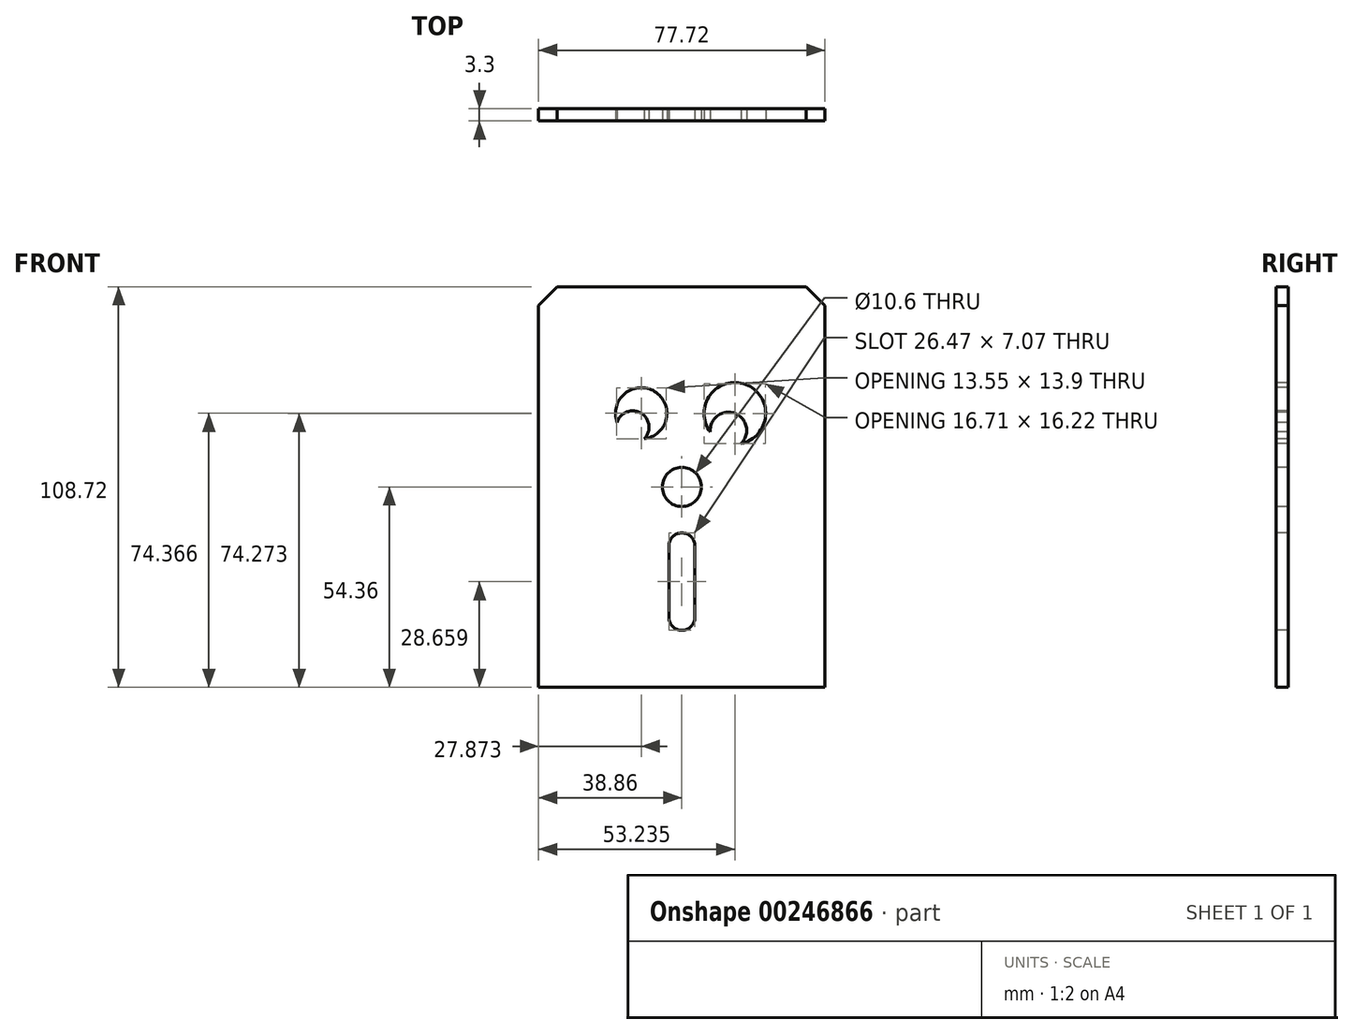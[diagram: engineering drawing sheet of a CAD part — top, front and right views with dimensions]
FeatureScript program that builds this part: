
annotation { "Feature Type Name" : "Feature", "Feature Type Description" : "" }
export const myFeature = defineFeature(function(context is Context, id is Id, definition is map)
    precondition{}
    {
        {
            var Q0;
            Q0=qCreatedBy(makeId("Front.planeOp"),FACE);
            var sketch = newSketch(context, id + "F0", { "sketchPlane" : qUnion([Q0])});
            skLineSegment(sketch, "E0.bottom", {"start": v(38.86, 54.36) * mm, "end": v(-38.86, 54.36) * mm});
            skLineSegment(sketch, "E0.top", {"start": v(38.86, -54.36) * mm, "end": v(-38.86, -54.36) * mm});
            skLineSegment(sketch, "E0.left", {"start": v(38.86, 54.36) * mm, "end": v(38.86, -54.36) * mm});
            skLineSegment(sketch, "E0.right", {"start": v(-38.86, 54.36) * mm, "end": v(-38.86, -54.36) * mm});
            skPoint(sketch, "E0.middle", {"position": v(0, 0) * mm});
            skSolve(sketch);
        }
        {
            var Q0;
            Q0=qSketchRegion(id+"F0",true);
            extrude(context, id + "F1", {"entities" : qUnion([Q0]), "depth" : 3.3 * mm});
        }
        {
            var Q0;
            Q0=makeQuery(id+"F1.opExtrude","CAP_FACE",FACE,{"disambiguationData":[OSD([sQuery(id+"F0.wireOp",EDGE,"E0.bottom"),sQuery(id+"F0.wireOp",EDGE,"E0.top"),sQuery(id+"F0.wireOp",EDGE,"E0.left"),sQuery(id+"F0.wireOp",EDGE,"E0.right")])],"isStart":false});
            var sketch = newSketch(context, id + "F2", { "sketchPlane" : qUnion([Q0])});
            skLineSegment(sketch, "E1", {"start": v(0, 57.24) * mm, "end": v(0, -57.24) * mm, "construction": true});
            skLineSegment(sketch, "E2", {"start": v(-50.8, 0) * mm, "end": v(50.8, 0) * mm, "construction": true});
            skArc(sketch, "E3", {"start": v(35.44, -3.57) * mm, "mid": v(31.46, -11.87) * mm, "end": v(32.26, -21.03) * mm});
            skLineSegment(sketch, "E4", {"start": v(15.88, -44.54) * mm, "end": v(0, -44.54) * mm, "construction": true});
            skArc(sketch, "E5", {"start": v(15.88, -44.54) * mm, "mid": v(30.2, -37.06) * mm, "end": v(32.26, -21.03) * mm});
            skArc(sketch, "E6", {"start": v(15.88, -44.54) * mm, "mid": v(7.78, -45.34) * mm, "end": v(0, -47.71) * mm});
            skArc(sketch, "E7.MirrorCS", {"start": v(-15.87, -44.54) * mm, "mid": v(-7.78, -45.34) * mm, "end": v(0, -47.71) * mm});
            skArc(sketch, "E8.MirrorCS", {"start": v(-15.87, -44.54) * mm, "mid": v(-30.2, -37.06) * mm, "end": v(-32.26, -21.03) * mm});
            skArc(sketch, "E9.MirrorCS", {"start": v(-35.44, -3.57) * mm, "mid": v(-31.46, -11.87) * mm, "end": v(-32.26, -21.03) * mm});
            skArc(sketch, "E10.MirrorCS", {"start": v(-35.44, 3.57) * mm, "mid": v(-31.46, 11.87) * mm, "end": v(-32.26, 21.03) * mm});
            skArc(sketch, "E11.MirrorCS", {"start": v(-15.88, 44.54) * mm, "mid": v(-30.2, 37.06) * mm, "end": v(-32.26, 21.03) * mm});
            skArc(sketch, "E12.MirrorCS", {"start": v(-15.88, 44.54) * mm, "mid": v(-7.78, 45.34) * mm, "end": v(0, 47.71) * mm});
            skArc(sketch, "E13.MirrorCS", {"start": v(15.87, 44.54) * mm, "mid": v(7.78, 45.34) * mm, "end": v(0, 47.71) * mm});
            skArc(sketch, "E14.MirrorCS", {"start": v(15.87, 44.54) * mm, "mid": v(30.2, 37.06) * mm, "end": v(32.26, 21.03) * mm});
            skArc(sketch, "E15.MirrorCS", {"start": v(35.44, 3.57) * mm, "mid": v(31.46, 11.87) * mm, "end": v(32.26, 21.03) * mm});
            skArc(sketch, "E16", {"start": v(35.44, 3.57) * mm, "mid": v(34.41, 0) * mm, "end": v(35.44, -3.57) * mm});
            skPoint(sketch, "E17.orphan", {"position": v(39.69, 0) * mm});
            skArc(sketch, "E18.MirrorCS", {"start": v(-35.44, 3.57) * mm, "mid": v(-34.41, 0) * mm, "end": v(-35.44, -3.57) * mm});
            skPoint(sketch, "E19.orphan", {"position": v(-39.69, 0) * mm});
            skSolve(sketch);
        }
        {
            var Q0;
            Q0=makeQuery(id+"F2.imprint","IMPRINT",FACE,{"disambiguationData":[TD([[makeQuery(id+"F2.imprint","IMPRINT",EDGE,{"derivedFrom":sQuery(id+"F2.wireOp",EDGE,"E3")}),1.0]])]});
            var sketch = newSketch(context, id + "F3", { "sketchPlane" : qUnion([Q0])});
            skFitSpline(sketch, "E20", {"points": [v(-34.74, -25) * mm, v(-17.68, -23.14) * mm, v(0, -25.84) * mm, v(18.3, -28) * mm, v(33.6, -24.4) * mm], "startDerivative": vector(68.08, 28.42) * mm, "endDerivative": vector(41.75, 55.86) * mm});
            skArc(sketch, "E21.0", {"start": v(15.88, -44.54) * mm, "mid": v(28.97, -38.63) * mm, "end": v(33.2, -24.9) * mm});
            skArc(sketch, "E22.0", {"start": v(-15.87, -44.54) * mm, "mid": v(-29.14, -38.43) * mm, "end": v(-33.13, -24.38) * mm});
            skArc(sketch, "E23.0", {"start": v(15.88, -44.54) * mm, "mid": v(7.78, -45.34) * mm, "end": v(0, -47.71) * mm});
            skArc(sketch, "E23.1", {"start": v(-15.87, -44.54) * mm, "mid": v(-7.78, -45.34) * mm, "end": v(0, -47.71) * mm});
            skPoint(sketch, "E24.orphan", {"position": v(-32.26, -21.03) * mm});
            skLineSegment(sketch, "E25.bottom", {"start": v(23.58, -32.65) * mm, "end": v(5.44, -32.65) * mm, "construction": true});
            skLineSegment(sketch, "E25.top", {"start": v(23.58, -12.55) * mm, "end": v(5.44, -12.55) * mm, "construction": true});
            skLineSegment(sketch, "E25.left", {"start": v(23.58, -32.65) * mm, "end": v(23.58, -12.55) * mm, "construction": true});
            skLineSegment(sketch, "E25.right", {"start": v(5.44, -32.65) * mm, "end": v(5.44, -12.55) * mm, "construction": true});
            skArc(sketch, "E26", {"start": v(6.5, -26.77) * mm, "mid": v(6.6, -19.6) * mm, "end": v(5.44, -12.55) * mm});
            skArc(sketch, "E27", {"start": v(23.58, -12.55) * mm, "mid": v(22.47, -20.37) * mm, "end": v(22.78, -28.26) * mm});
            skLineSegment(sketch, "E28", {"start": v(0.57, -13.45) * mm, "end": v(5.44, -12.55) * mm});
            skLineSegment(sketch, "E29", {"start": v(28.46, 0) * mm, "end": v(0.57, 0) * mm, "construction": true});
            skArc(sketch, "E30", {"start": v(-2.4, -8.48) * mm, "mid": v(-2.65, -12) * mm, "end": v(0.57, -13.45) * mm});
            skArc(sketch, "E31", {"start": v(0, -10.42) * mm, "mid": v(-0.23, -8.24) * mm, "end": v(-2.4, -8.48) * mm});
            skArc(sketch, "E32", {"start": v(0, -10.42) * mm, "mid": v(-0.04, -11.92) * mm, "end": v(1.4, -12.35) * mm});
            skArc(sketch, "E33", {"start": v(1.4, -12.35) * mm, "mid": v(5.55, -5.86) * mm, "end": v(0.57, 0) * mm});
            skLineSegment(sketch, "E34", {"start": v(14.51, 0) * mm, "end": v(14.51, -12.55) * mm, "construction": true});
            skArc(sketch, "E35.MirrorCS", {"start": v(27.61, -12.35) * mm, "mid": v(23.47, -5.86) * mm, "end": v(28.46, 0) * mm});
            skLineSegment(sketch, "E36.MirrorCS", {"start": v(28.46, -13.45) * mm, "end": v(23.58, -12.55) * mm});
            skArc(sketch, "E37.MirrorCS", {"start": v(31.42, -8.48) * mm, "mid": v(31.67, -12) * mm, "end": v(28.46, -13.45) * mm});
            skArc(sketch, "E38.MirrorCS", {"start": v(29.02, -10.42) * mm, "mid": v(29.25, -8.24) * mm, "end": v(31.42, -8.48) * mm});
            skArc(sketch, "E39.MirrorCS", {"start": v(29.02, -10.42) * mm, "mid": v(29.06, -11.92) * mm, "end": v(27.61, -12.35) * mm});
            skArc(sketch, "E40", {"start": v(0.57, 0) * mm, "mid": v(5.65, -0.6) * mm, "end": v(10.76, -0.93) * mm});
            skLineSegment(sketch, "E41", {"start": v(10.76, -0.93) * mm, "end": v(8.47, 9.06) * mm});
            skLineSegment(sketch, "E42", {"start": v(8.47, 9.06) * mm, "end": v(6.8, 8.68) * mm});
            skArc(sketch, "E43", {"start": v(7.7, 9.94) * mm, "mid": v(5.6, 10.49) * mm, "end": v(6.8, 8.68) * mm});
            skLineSegment(sketch, "E44", {"start": v(14.51, 0) * mm, "end": v(14.77, 8.31) * mm, "construction": true});
            skLineSegment(sketch, "E45.MirrorCS", {"start": v(18.26, -0.93) * mm, "end": v(21.1, 8.66) * mm});
            skLineSegment(sketch, "E46.MirrorCS", {"start": v(21.1, 8.66) * mm, "end": v(22.75, 8.18) * mm});
            skArc(sketch, "E47.MirrorCS", {"start": v(21.93, 9.5) * mm, "mid": v(24.07, 9.9) * mm, "end": v(22.75, 8.18) * mm});
            skArc(sketch, "E48", {"start": v(7.7, 9.94) * mm, "mid": v(12.62, 15.22) * mm, "end": v(14.1, 22.28) * mm});
            skArc(sketch, "E49", {"start": v(15.59, 22.28) * mm, "mid": v(17.1, 15.06) * mm, "end": v(21.93, 9.5) * mm});
            skLineSegment(sketch, "E50", {"start": v(14.1, 22.28) * mm, "end": v(12.75, 29.94) * mm});
            skLineSegment(sketch, "E51", {"start": v(12.75, 29.94) * mm, "end": v(10.25, 29.5) * mm});
            skLineSegment(sketch, "E52", {"start": v(10.25, 29.5) * mm, "end": v(10.04, 30.72) * mm});
            skLineSegment(sketch, "E53", {"start": v(10.04, 30.72) * mm, "end": v(12.66, 31.3) * mm});
            skLineSegment(sketch, "E54", {"start": v(12.66, 31.3) * mm, "end": v(12.12, 34.79) * mm});
            skLineSegment(sketch, "E55", {"start": v(12.12, 34.79) * mm, "end": v(14.24, 35.11) * mm});
            skLineSegment(sketch, "E56", {"start": v(14.24, 35.11) * mm, "end": v(14.8, 31.45) * mm});
            skLineSegment(sketch, "E57", {"start": v(14.8, 31.45) * mm, "end": v(17.72, 31.9) * mm});
            skLineSegment(sketch, "E58", {"start": v(17.72, 31.9) * mm, "end": v(17.99, 30.17) * mm});
            skLineSegment(sketch, "E59", {"start": v(17.99, 30.17) * mm, "end": v(14.89, 29.68) * mm});
            skLineSegment(sketch, "E60", {"start": v(14.89, 29.68) * mm, "end": v(15.59, 22.28) * mm});
            skArc(sketch, "E61.trimOffspring", {"start": v(18.26, -0.93) * mm, "mid": v(23.37, -0.6) * mm, "end": v(28.46, 0) * mm});
            skPoint(sketch, "E62.orphan", {"position": v(18.2, -1.17) * mm});
            skLineSegment(sketch, "E63", {"start": v(8.48, -4.98) * mm, "end": v(9.12, -7.41) * mm});
            skLineSegment(sketch, "E64", {"start": v(9.77, -9.85) * mm, "end": v(10.94, -9.54) * mm});
            skLineSegment(sketch, "E65", {"start": v(12.72, -9.06) * mm, "end": v(12.26, -7.34) * mm});
            skLineSegment(sketch, "E66", {"start": v(11.56, -4.7) * mm, "end": v(10.33, -4.82) * mm});
            skLineSegment(sketch, "E67", {"start": v(9.75, -4.87) * mm, "end": v(10.34, -7.13) * mm});
            skLineSegment(sketch, "E68", {"start": v(10.34, -7.13) * mm, "end": v(9.12, -7.41) * mm});
            skLineSegment(sketch, "E69", {"start": v(10.33, -4.82) * mm, "end": v(10.9, -7.06) * mm});
            skLineSegment(sketch, "E70", {"start": v(10.9, -7.06) * mm, "end": v(12.14, -6.89) * mm});
            skLineSegment(sketch, "E71", {"start": v(9.29, -8.05) * mm, "end": v(10.46, -7.73) * mm});
            skLineSegment(sketch, "E72", {"start": v(10.46, -7.73) * mm, "end": v(10.94, -9.54) * mm});
            skLineSegment(sketch, "E73", {"start": v(11.57, -9.37) * mm, "end": v(11.12, -7.64) * mm});
            skLineSegment(sketch, "E74", {"start": v(11.12, -7.64) * mm, "end": v(12.26, -7.34) * mm});
            skLineSegment(sketch, "E75.trimOffspring", {"start": v(12.14, -6.89) * mm, "end": v(11.56, -4.7) * mm});
            skLineSegment(sketch, "E76.trimOffspring", {"start": v(9.75, -4.87) * mm, "end": v(8.48, -4.98) * mm});
            skLineSegment(sketch, "E77.trimOffspring", {"start": v(9.29, -8.05) * mm, "end": v(9.77, -9.85) * mm});
            skLineSegment(sketch, "E78.trimOffspring", {"start": v(11.57, -9.37) * mm, "end": v(12.72, -9.06) * mm});
            skLineSegment(sketch, "E79.MirrorCS", {"start": v(17.46, -4.7) * mm, "end": v(18.69, -4.82) * mm});
            skLineSegment(sketch, "E80.MirrorCS", {"start": v(19.27, -4.87) * mm, "end": v(18.68, -7.13) * mm});
            skLineSegment(sketch, "E81.MirrorCS", {"start": v(17.45, -9.37) * mm, "end": v(17.9, -7.64) * mm});
            skLineSegment(sketch, "E82.MirrorCS", {"start": v(18.68, -7.13) * mm, "end": v(19.9, -7.41) * mm});
            skLineSegment(sketch, "E83.MirrorCS", {"start": v(17.9, -7.64) * mm, "end": v(16.76, -7.34) * mm});
            skLineSegment(sketch, "E84.MirrorCS", {"start": v(18.69, -4.82) * mm, "end": v(18.12, -7.06) * mm});
            skLineSegment(sketch, "E85.MirrorCS", {"start": v(16.88, -6.89) * mm, "end": v(17.46, -4.7) * mm});
            skLineSegment(sketch, "E86.MirrorCS", {"start": v(18.12, -7.06) * mm, "end": v(16.88, -6.89) * mm});
            skLineSegment(sketch, "E87.MirrorCS", {"start": v(19.27, -4.87) * mm, "end": v(20.54, -4.98) * mm});
            skLineSegment(sketch, "E88.MirrorCS", {"start": v(20.54, -4.98) * mm, "end": v(19.9, -7.41) * mm});
            skLineSegment(sketch, "E89.MirrorCS", {"start": v(19.73, -8.05) * mm, "end": v(18.56, -7.73) * mm});
            skLineSegment(sketch, "E90.MirrorCS", {"start": v(19.73, -8.05) * mm, "end": v(19.25, -9.85) * mm});
            skLineSegment(sketch, "E91.MirrorCS", {"start": v(19.25, -9.85) * mm, "end": v(18.08, -9.54) * mm});
            skLineSegment(sketch, "E92.MirrorCS", {"start": v(18.56, -7.73) * mm, "end": v(18.08, -9.54) * mm});
            skLineSegment(sketch, "E93.MirrorCS", {"start": v(17.45, -9.37) * mm, "end": v(16.3, -9.06) * mm});
            skLineSegment(sketch, "E94.MirrorCS", {"start": v(16.3, -9.06) * mm, "end": v(16.76, -7.34) * mm});
            skArc(sketch, "E95", {"start": v(14.28, 11.97) * mm, "mid": v(12.23, 10.98) * mm, "end": v(11.15, 8.98) * mm});
            skLineSegment(sketch, "E96", {"start": v(14.28, 11.97) * mm, "end": v(14.28, 8.98) * mm});
            skLineSegment(sketch, "E97", {"start": v(15.17, 4.65) * mm, "end": v(15.17, 7.88) * mm});
            skLineSegment(sketch, "E98", {"start": v(18.4, 8.98) * mm, "end": v(15.17, 8.98) * mm});
            skLineSegment(sketch, "E99", {"start": v(11.1, 7.88) * mm, "end": v(14.28, 7.88) * mm});
            skLineSegment(sketch, "E100.trimOffspring", {"start": v(15.17, 8.98) * mm, "end": v(15.17, 11.98) * mm});
            skLineSegment(sketch, "E101.trimOffspring", {"start": v(15.17, 7.88) * mm, "end": v(18.43, 7.88) * mm});
            skLineSegment(sketch, "E102.trimOffspring", {"start": v(14.28, 7.88) * mm, "end": v(14.28, 4.66) * mm});
            skLineSegment(sketch, "E103.trimOffspring", {"start": v(14.28, 8.98) * mm, "end": v(11.15, 8.98) * mm});
            skArc(sketch, "E104.trimOffspring", {"start": v(11.1, 7.88) * mm, "mid": v(12.14, 5.73) * mm, "end": v(14.28, 4.66) * mm});
            skArc(sketch, "E105.trimOffspring", {"start": v(18.4, 8.98) * mm, "mid": v(17.28, 11.01) * mm, "end": v(15.17, 11.98) * mm});
            skArc(sketch, "E106.trimOffspring", {"start": v(15.17, 4.65) * mm, "mid": v(17.37, 5.7) * mm, "end": v(18.43, 7.88) * mm});
            skLineSegment(sketch, "E107.left", {"start": v(12.04, -27.4) * mm, "end": v(12.04, -21.48) * mm});
            skLineSegment(sketch, "E107.right", {"start": v(16, -27.8) * mm, "end": v(16, -21.48) * mm});
            skArc(sketch, "E108", {"start": v(16, -21.48) * mm, "mid": v(14.02, -19.5) * mm, "end": v(12.04, -21.48) * mm});
            skLineSegment(sketch, "E109", {"start": v(12.04, -27.4) * mm, "end": v(16, -27.8) * mm});
            skArc(sketch, "E110.0", {"start": v(-35.44, -3.57) * mm, "mid": v(-31.46, -11.87) * mm, "end": v(-32.26, -21.03) * mm, "construction": true});
            skArc(sketch, "E110.1", {"start": v(15.87, 44.54) * mm, "mid": v(7.78, 45.34) * mm, "end": v(0, 47.71) * mm});
            skArc(sketch, "E110.2", {"start": v(-15.88, 44.54) * mm, "mid": v(-30.2, 37.06) * mm, "end": v(-32.26, 21.03) * mm, "construction": true});
            skArc(sketch, "E110.3", {"start": v(-35.44, 3.57) * mm, "mid": v(-34.41, 0) * mm, "end": v(-35.44, -3.57) * mm, "construction": true});
            skArc(sketch, "E110.4", {"start": v(-35.44, 3.57) * mm, "mid": v(-31.46, 11.87) * mm, "end": v(-32.26, 21.03) * mm});
            skArc(sketch, "E110.5", {"start": v(-15.88, 44.54) * mm, "mid": v(-7.78, 45.34) * mm, "end": v(0, 47.71) * mm});
            skArc(sketch, "E111", {"start": v(-17.1, 9.66) * mm, "mid": v(-3.37, 14.89) * mm, "end": v(1.5, 28.74) * mm});
            skArc(sketch, "E112", {"start": v(-17.1, 9.66) * mm, "mid": v(-26.87, 8.42) * mm, "end": v(-35.44, 3.57) * mm});
            skArc(sketch, "E113", {"start": v(15.87, 44.54) * mm, "mid": v(5.2, 39.82) * mm, "end": v(1.5, 28.74) * mm});
            skArc(sketch, "E114.trimOffspring", {"start": v(-15.88, 44.54) * mm, "mid": v(-30.2, 37.06) * mm, "end": v(-32.26, 21.03) * mm});
            skArc(sketch, "E115", {"start": v(-24.92, -22.89) * mm, "mid": v(-23.55, -16.2) * mm, "end": v(-24.4, -9.44) * mm});
            skFitSpline(sketch, "E116", {"points": [v(-24.4, -9.44) * mm, v(-26.98, -10.38) * mm, v(-27.97, -8.39) * mm, v(-29.93, -8.52) * mm, v(-30.92, -6) * mm, v(-32.1, -5.52) * mm, v(-32.53, -4.18) * mm, v(-32.18, -3.27) * mm, v(-31.84, -4.44) * mm, v(-31.05, -4.83) * mm, v(-31.49, -2) * mm, v(-30.88, -2.14) * mm, v(-30.1, -5.05) * mm, v(-29.45, -3.57) * mm, v(-28.71, -3.66) * mm, v(-29.54, -5.78) * mm, v(-29.23, -7.17) * mm, v(-27.54, -7.04) * mm, v(-26.28, -8.52) * mm, v(-24.4, -7.6) * mm], "startDerivative": vector(-46.53, -30.94) * mm, "endDerivative": vector(36.03, 29.74) * mm});
            skArc(sketch, "E117", {"start": v(-24.4, -7.6) * mm, "mid": v(-24.93, -4.98) * mm, "end": v(-25.9, -2.49) * mm});
            skFitSpline(sketch, "E118", {"points": [v(-25.9, -2.49) * mm, v(-27.5, -1.49) * mm, v(-28.76, -1.49) * mm, v(-29.23, 0) * mm, v(-31.14, 0) * mm, v(-30.8, 3.42) * mm, v(-29.97, 3.55) * mm, v(-30.27, 1.77) * mm, v(-29.54, 1.72) * mm, v(-28.8, 4.59) * mm, v(-27.67, 4.37) * mm, v(-28.28, 1.98) * mm, v(-27.84, 0) * mm, v(-27.2, 2.46) * mm, v(-25.9, 2.37) * mm, v(-25.9, 0) * mm, v(-24.11, -2.49) * mm, v(-22.72, -5.26) * mm, v(-21.68, -4.18) * mm, v(-23.16, 1.33) * mm, v(-20.82, 1.46) * mm, v(-20.82, 3.02) * mm], "startDerivative": vector(-33.14, 31.82) * mm, "endDerivative": vector(-15.18, 49.9) * mm});
            skFitSpline(sketch, "E119", {"points": [v(-20.82, 3.02) * mm, v(-19.2, 3.92) * mm, v(-20.04, 5.84) * mm, v(-20.82, 8.3) * mm, v(-20.04, 8.38) * mm, v(-19.62, 6.46) * mm, v(-18.62, 5.34) * mm, v(-18.96, 7.3) * mm, v(-18.2, 7.55) * mm, v(-18.12, 4.13) * mm, v(-19.33, 2.25) * mm, v(-19.46, 0.87) * mm, v(-20.82, 0) * mm, v(-20.04, -3.35) * mm, v(-16.32, 0) * mm, v(-17.1, 1.46) * mm, v(-15.74, 3.02) * mm, v(-15.45, 5.84) * mm, v(-14.49, 5.55) * mm, v(-14.82, 3.02) * mm, v(-14.53, 1.46) * mm, v(-13.36, 4) * mm, v(-12.02, 3.02) * mm, v(-14.2, 0) * mm, v(-17.1, -4.06) * mm, v(-17.1, -7.4) * mm, v(-14.36, -5.44) * mm, v(-14.57, -4.1) * mm, v(-12.78, -3.22) * mm, v(-12.53, -1.68) * mm, v(-10.44, -0.8) * mm, v(-10.27, 1.46) * mm, v(-9.35, 0) * mm, v(-8.6, 3.02) * mm, v(-8.1, 0) * mm, v(-9.44, -1.26) * mm, v(-11.31, -3.26) * mm, v(-13.15, -4.6) * mm, v(-13.36, -6.6) * mm, v(-15.78, -8.94) * mm], "startDerivative": vector(94.65, 30.69) * mm, "endDerivative": vector(-102.82, -69.25) * mm});
            skArc(sketch, "E120", {"start": v(-15.78, -8.94) * mm, "mid": v(-16.8, -16.14) * mm, "end": v(-15.78, -23.34) * mm});
            skFitSpline(sketch, "E121", {"points": [v(-22.4, -11.55) * mm, v(-21.43, -13.07) * mm, v(-21.4, -14.11) * mm, v(-20.72, -14.36) * mm, v(-20.54, -13.59) * mm, v(-20.94, -12.02) * mm, v(-21.71, -11.06) * mm, v(-22.67, -10.07) * mm, v(-22.4, -11.55) * mm]});
            skFitSpline(sketch, "E122", {"points": [v(-18.38, -10.1) * mm, v(-19.09, -11.5) * mm, v(-19.21, -12.7) * mm, v(-19.15, -14.02) * mm, v(-18.84, -14.6) * mm, v(-18.38, -14.05) * mm, v(-18.26, -13.1) * mm, v(-18.56, -12.32) * mm, v(-18.29, -11.28) * mm, v(-17.6, -10.38) * mm, v(-18.38, -10.1) * mm]});
            skFitSpline(sketch, "E123", {"points": [v(-20.3, -15.78) * mm, v(-20.35, -17.1) * mm, v(-20.9, -18.47) * mm, v(-21.8, -19.67) * mm, v(-21.9, -21.46) * mm, v(-20.45, -21.43) * mm, v(-19.64, -20.38) * mm, v(-19.43, -18.84) * mm, v(-19.7, -17.85) * mm, v(-19.7, -16.37) * mm, v(-19.43, -15.38) * mm, v(-20.3, -15.78) * mm]});
            skCircle(sketch, "E124", {"center": v(-15.88, 27.08) * mm, "radius": 13.34 * mm});
            skSolve(sketch);
        }
        {
            var Q0;
            Q0=qSketchRegion(id+"F3",true);
            extrude(context, id + "F4", {"entities" : qUnion([Q0]), "operationType" : NewBodyOperationType.ADD, "oppositeDirection" : true, "depth" : 3.3 * mm});
        }
        {
            var Q0;
            Q0=makeQuery(id+"F1.opExtrude","SWEPT_EDGE",EDGE,{"disambiguationData":[OSD([sQuery(id+"F0.wireOp",EDGE,"E0.bottom"),sQuery(id+"F0.wireOp",EDGE,"E0.right")])]});
            var Q1;
            Q1=makeQuery(id+"F1.opExtrude","SWEPT_EDGE",EDGE,{"disambiguationData":[OSD([sQuery(id+"F0.wireOp",EDGE,"E0.bottom"),sQuery(id+"F0.wireOp",EDGE,"E0.left")])]});
            chamfer(context, id + "F5", {"entities" : qUnion([Q0, Q1]), "width" : 5.08 * mm, "tangentPropagation" : true});
        }
        {
            var Q0;
            Q0=makeQuery(id+"F2.imprint","IMPRINT",FACE,{"disambiguationData":[TD([[makeQuery(id+"F2.imprint","IMPRINT",EDGE,{"derivedFrom":sQuery(id+"F2.wireOp",EDGE,"E3")}),-1.0]])]});
            var sketch = newSketch(context, id + "F6", { "sketchPlane" : qUnion([Q0])});
            skArc(sketch, "E125", {"start": v(16.1, 11.8) * mm, "mid": v(17.33, 27.82) * mm, "end": v(7.7, 14.96) * mm});
            skArc(sketch, "E126", {"start": v(-10.25, 13.05) * mm, "mid": v(-7.36, 25.93) * mm, "end": v(-17.57, 17.57) * mm});
            skArc(sketch, "E127", {"start": v(16.1, 11.8) * mm, "mid": v(14.39, 20) * mm, "end": v(7.7, 14.96) * mm});
            skArc(sketch, "E128", {"start": v(-10.25, 13.05) * mm, "mid": v(-11.02, 20) * mm, "end": v(-17.57, 17.57) * mm});
            skCircle(sketch, "E129", {"center": v(0, 0) * mm, "radius": 5.3 * mm});
            skLineSegment(sketch, "E130.bottom", {"start": v(3.53, -16) * mm, "end": v(-3.53, -16) * mm, "construction": true});
            skLineSegment(sketch, "E130.top", {"start": v(3.53, -35.4) * mm, "end": v(-3.53, -35.4) * mm, "construction": true});
            skLineSegment(sketch, "E130.left", {"start": v(3.53, -16) * mm, "end": v(3.53, -35.4) * mm});
            skLineSegment(sketch, "E130.right", {"start": v(-3.53, -16) * mm, "end": v(-3.53, -35.4) * mm});
            skPoint(sketch, "E130.middle", {"position": v(0, -25.7) * mm});
            skArc(sketch, "E131", {"start": v(3.53, -16) * mm, "mid": v(0, -12.47) * mm, "end": v(-3.53, -16) * mm});
            skArc(sketch, "E132", {"start": v(-3.53, -35.4) * mm, "mid": v(0, -38.93) * mm, "end": v(3.53, -35.4) * mm});
            skSolve(sketch);
        }
        {
            var Q0;
            Q0=qSketchRegion(id+"F6",true);
            extrude(context, id + "F7", {"entities" : qUnion([Q0]), "operationType" : NewBodyOperationType.REMOVE, "endBound" : BoundingType.THROUGH_ALL, "oppositeDirection" : true, "depth" : 25.4 * mm});
        }
    });
